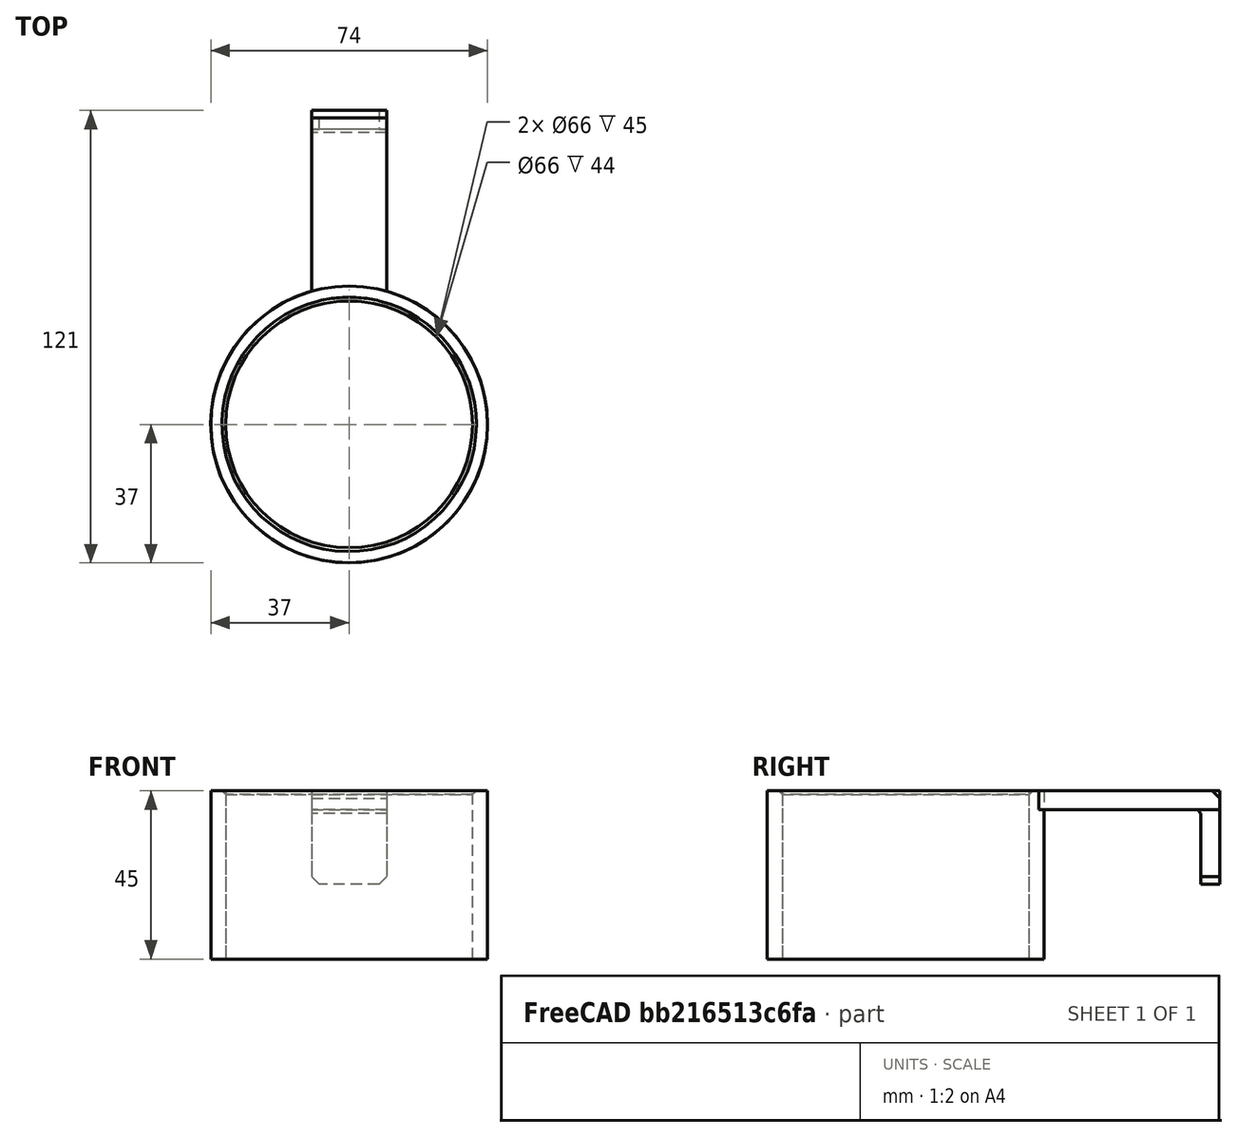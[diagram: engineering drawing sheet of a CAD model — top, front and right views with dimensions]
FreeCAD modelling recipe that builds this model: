
FCSTD DOCUMENT  (FreeCAD 0.16R)
Label: AbbeyCupHolder
License: All rights reserved
LicenseURL: http://en.wikipedia.org/wiki/All_rights_reserved
objects: PartDesign::Chamfer×4, Sketcher::SketchObject×3, PartDesign::Pad×3, Mesh::Feature×1
note: 13 computed .brp shape members not serialized (recipe doc carries the construction recipe); baked Part::Feature solids carry a one-line shape summary decoded from their .brp

FEATURE [Sketcher::SketchObject] Sketch
  sketch-geometry (2):
    g0: Circle CenterX=0 CenterY=0 CenterZ=0 NormalX=0 NormalY=0 NormalZ=1 Radius=33
    g1: Circle CenterX=0 CenterY=0 CenterZ=0 NormalX=0 NormalY=0 NormalZ=1 Radius=37
  constraints (4):
    c: Coincident(g0,g-1)
    c: Coincident(g1,g-1)
    c: Radius(g0) = 33
    c: Radius(g1) = 37
FEATURE [PartDesign::Pad] Pad
  Length = 45
  Length2 = 100
  Sketch = -> Sketch
  Type = 0
FEATURE [Sketcher::SketchObject] Sketch001
  ExternalGeometry = -> [Pad]
  Placement = pos=(0,0,45) rot=(0,0,1;0rad)
  Support = -> Pad [Face4]
  sketch-geometry (4):
    g0: LineSegment StartX=-10 StartY=84 StartZ=0 EndX=10 EndY=84 EndZ=0
    g1: LineSegment StartX=10 StartY=84 StartZ=0 EndX=10 EndY=33 EndZ=0
    g2: LineSegment StartX=10 StartY=33 StartZ=0 EndX=-10 EndY=33 EndZ=0
    g3: LineSegment StartX=-10 StartY=33 StartZ=0 EndX=-10 EndY=84 EndZ=0
  constraints (12):
    c: Coincident(g0,g1)
    c: Coincident(g1,g2)
    c: Coincident(g2,g3)
    c: Coincident(g3,g0)
    c: Horizontal(g0)
    c: Horizontal(g2)
    c: Vertical(g1)
    c: Vertical(g3)
    c: Symmetric(g1,g2,g-2)
    c: Distance(g2) = 20
    c: DistanceY(g1,g1) = 51
    c: Tangent(g2,g-4)
FEATURE [PartDesign::Pad] Pad001
  Length = 5
  Length2 = 100
  Reversed = true
  Sketch = -> Sketch001
  Type = 0
FEATURE [Sketcher::SketchObject] Sketch002
  ExternalGeometry = -> [Pad001]
  Placement = pos=(0,0,40) rot=(1,0,0;3.14159rad)
  Support = -> Pad001 [Face6]
  sketch-geometry (4):
    g0: LineSegment StartX=10 StartY=-79 StartZ=0 EndX=-10 EndY=-79 EndZ=0
    g1: LineSegment StartX=-10 StartY=-79 StartZ=0 EndX=-10 EndY=-84 EndZ=0
    g2: LineSegment StartX=-10 StartY=-84 StartZ=0 EndX=10 EndY=-84 EndZ=0
    g3: LineSegment StartX=10 StartY=-84 StartZ=0 EndX=10 EndY=-79 EndZ=0
  constraints (11):
    c: Coincident(g0,g1)
    c: Coincident(g1,g2)
    c: Coincident(g2,g3)
    c: Coincident(g3,g0)
    c: Horizontal(g0)
    c: Horizontal(g2)
    c: Vertical(g1)
    c: Vertical(g3)
    c: Coincident(g2,g-3)
    c: Coincident(g1,g-3)
    c: Distance(g3) = 5
FEATURE [PartDesign::Pad] Pad002
  Length = 20
  Length2 = 100
  Sketch = -> Sketch002
  Type = 0
FEATURE [PartDesign::Chamfer] Chamfer
  Base = -> Pad002 [Edge10]
  Size = 1
FEATURE [PartDesign::Chamfer] Chamfer001
  Base = -> Chamfer [Edge34]
  Size = 2
FEATURE [PartDesign::Chamfer] Chamfer002
  Base = -> Chamfer001 [Edge21]
  Size = 1
FEATURE [PartDesign::Chamfer] Chamfer003
  Base = -> Chamfer002 [Edge34,Edge13]
  Size = 2
FEATURE [Mesh::Feature] Mesh  label="Chamfer003 (Meshed)"
